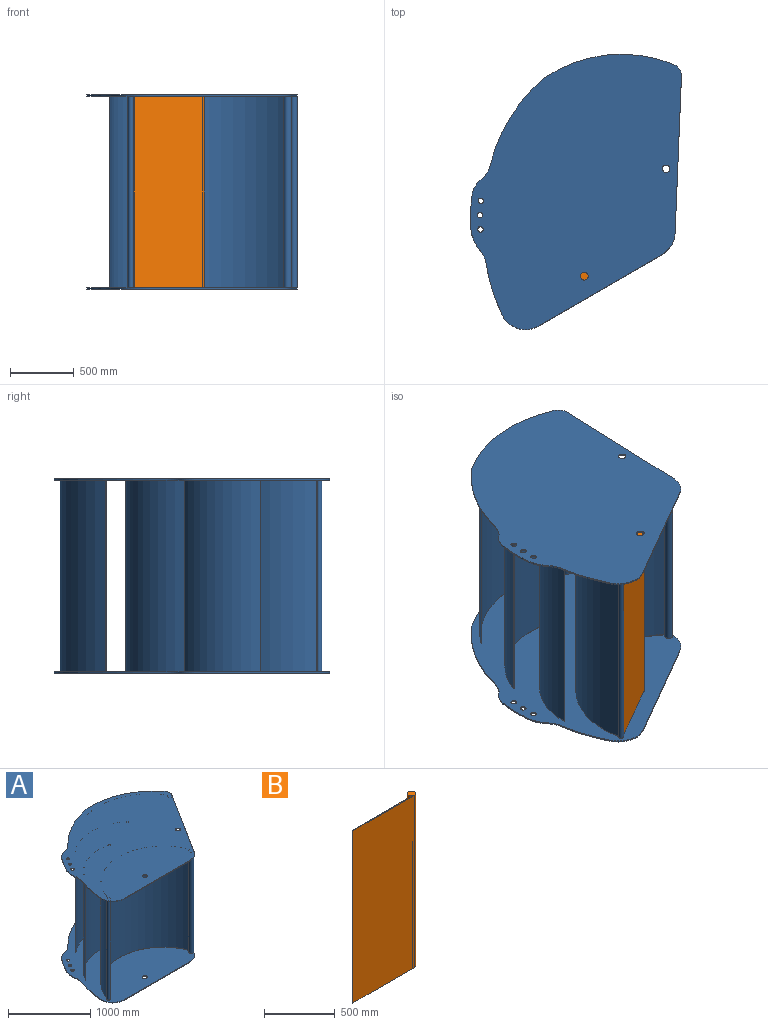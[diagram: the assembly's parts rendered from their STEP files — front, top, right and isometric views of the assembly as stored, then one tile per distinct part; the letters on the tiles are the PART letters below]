
ASSEMBLY  parts=2 mates=2
PART A: 61 faces, bbox 2164.2x1661x1520 mm
  f0: cylinder r=30.5mm len=61mm, axis (0,0,-1), area 1916.4mm2, adj f48,f49
  f1: cylinder r=29.5mm len=59mm, axis (0,0,-1), area 1853.5mm2, adj f48,f49
  f2: cylinder r=22mm len=44mm, axis (0,0,-1), area 1382.3mm2, adj f48,f49
  f3: cylinder r=22mm len=44mm, axis (0,0,-1), area 1382.3mm2, adj f48,f49
  f4: cylinder r=22mm len=44mm, axis (0,0,-1), area 1382.3mm2, adj f48,f49
  f5: cylinder r=326.18mm len=176.61mm, axis (0,0,-1), area 1797.7mm2, adj f48,f49,f50,f60
  f6: cylinder r=200mm len=212.82mm, axis (0,0,-1), area 3269.9mm2, adj f48,f49,f51,f52
  f7: cylinder r=20.5mm len=1500mm, axis (0,0,-1), area 183146.8mm2, adj f30,f44,f45,f49
  f8: cylinder r=30.5mm len=1500mm, axis (0,0,-1), area 272705.4mm2, adj f30,f44,f45,f46,f47,f49
  f9: cylinder r=15.5mm len=1500mm, axis (0,0,-1), area 135747.8mm2, adj f30,f41,f43,f49
  f10: cylinder r=15.5mm len=1500mm, axis (0,0,-1), area 136340.4mm2, adj f30,f37,f40,f49
  f11: cylinder r=30.5mm len=1500mm, axis (0,0,-1), area 274743.1mm2, adj f30,f32,f34,f35,f36,f49
  f12: cylinder r=30.5mm len=61mm, axis (0,0,-1), area 1916.4mm2, adj f30,f31
  f13: cylinder r=22mm len=44mm, axis (0,0,-1), area 1382.3mm2, adj f30,f31
  f14: cylinder r=22mm len=44mm, axis (0,0,-1), area 1382.3mm2, adj f30,f31
  f15: cylinder r=22mm len=44mm, axis (0,0,-1), area 1382.3mm2, adj f30,f31
  f16: cylinder r=29.5mm len=59mm, axis (0,0,-1), area 1853.5mm2, adj f30,f31
  f17: cylinder r=326.18mm len=176.61mm, axis (0,0,-1), area 1797.7mm2, adj f28,f29,f30,f31
  f18: cylinder r=200mm len=212.82mm, axis (0,0,-1), area 3269.9mm2, adj f19,f20,f30,f31
  f19: cylinder r=1403.06mm len=415.74mm, axis (0,0,-1), area 4273.2mm2, adj f18,f29,f30,f31
  f20: plane 1123.76x10mm, normal (0,-1,0), area 11237.6mm2, adj f18,f21,f30,f31
  f21: cylinder r=200mm len=169mm, axis (0,0,-1), area 2013.2mm2, adj f20,f22,f30,f31
  f22: plane 1036.5x655.9mm, normal (0.85,-0.53,0), area 12265.9mm2, adj f21,f23,f30,f31,f36,f47
  f23: cylinder r=100mm len=114.68mm, axis (0,0,-1), area 1222.9mm2, adj f22,f24,f30,f31
  f24: cylinder r=1074.34mm len=926.41mm, axis (0,0,-1), area 10568mm2, adj f23,f25,f30,f31
  f25: cylinder r=1282.61mm len=713.26mm, axis (0,0,-1), area 8227.7mm2, adj f24,f26,f30,f31
  f26: cylinder r=200mm len=117.51mm, axis (0,0,-1), area 1346.6mm2, adj f25,f27,f30,f31
  f27: cylinder r=186.95mm len=116.81mm, axis (0,0,-1), area 1363.1mm2, adj f26,f28,f30,f31
  f28: cylinder r=1324.47mm len=239.75mm, axis (0,0,-1), area 2828.3mm2, adj f17,f27,f30,f31
  f29: cylinder r=200mm len=107.43mm, axis (0,0,-1), area 1093.1mm2, adj f17,f19,f30,f31
  f30: plane 2164.16x1660.98mm, normal (0,0,1), area 2565292.9mm2, adj f7,f8,f9,f10,f11,f12,f13,f14
  f31: plane 2164.16x1660.98mm, normal (0,0,-1), area 2603609.2mm2, adj f12,f13,f14,f15,f16,f17,f18,f19
  f32: cylinder r=883.17mm len=1500mm, axis (0,0,-1), area 1936048.7mm2, adj f11,f30,f33,f49
  f33: plane 1500x5.5mm, normal (-0.92,-0.4,0), area 9000mm2, adj f30,f32,f34,f49
  f34: cylinder r=877.17mm len=1500mm, axis (0,0,-1), area 1914005.6mm2, adj f11,f30,f33,f49
  f35: plane 9.3x5.88mm, normal (0,0,1), area 3.7mm2, adj f11,f54
  f36: plane 9.3x5.88mm, normal (0,0,-1), area 3.7mm2, adj f11,f22
  f37: cylinder r=685.89mm len=1500mm, axis (0,0,-1), area 1444091.5mm2, adj f10,f30,f38,f49
  f38: plane 1500x4.62mm, normal (-0.77,-0.64,0), area 9000mm2, adj f30,f37,f39,f49
  f39: plane 1500x0.08mm, normal (0.65,-0.76,0), area 152.6mm2, adj f30,f38,f40,f49
  f40: cylinder r=679.89mm len=1500mm, axis (0,0,-1), area 1427930.9mm2, adj f10,f30,f39,f49
  f41: cylinder r=640.37mm len=1500mm, axis (0,0,-1), area 1242581.2mm2, adj f9,f30,f42,f49
  f42: plane 1500x5.24mm, normal (-0.49,-0.87,0), area 9000mm2, adj f30,f41,f43,f49
  f43: cylinder r=634.37mm len=1500mm, axis (0,0,-1), area 1226053.6mm2, adj f9,f30,f42,f49
  f44: cylinder r=755.25mm len=1500mm, axis (0,0,-1), area 2799788.5mm2, adj f7,f8,f30,f49
  f45: cylinder r=761.25mm len=1500mm, axis (0,0,-1), area 2838096.4mm2, adj f7,f8,f30,f49
  f46: plane 9.3x5.88mm, normal (0,0,1), area 3.7mm2, adj f8,f54
  f47: plane 9.3x5.88mm, normal (0,0,-1), area 3.7mm2, adj f8,f22
  f48: plane 2164.16x1660.98mm, normal (0,0,1), area 2603609.2mm2, adj f0,f1,f2,f3,f4,f5,f6,f50
  f49: plane 2164.16x1660.98mm, normal (0,0,-1), area 2565292.9mm2, adj f0,f1,f2,f3,f4,f5,f6,f7
  f50: cylinder r=200mm len=107.43mm, axis (0,0,-1), area 1093.1mm2, adj f5,f48,f49,f51
  f51: cylinder r=1403.06mm len=415.74mm, axis (0,0,-1), area 4273.2mm2, adj f6,f48,f49,f50
  f52: plane 1123.76x10mm, normal (0,-1,0), area 11237.6mm2, adj f6,f48,f49,f53
  f53: cylinder r=200mm len=169mm, axis (0,0,-1), area 2013.2mm2, adj f48,f49,f52,f54
  f54: plane 1036.5x655.9mm, normal (0.85,-0.53,0), area 12265.9mm2, adj f35,f46,f48,f49,f53,f55
  f55: cylinder r=100mm len=114.68mm, axis (0,0,-1), area 1222.9mm2, adj f48,f49,f54,f56
  f56: cylinder r=1074.34mm len=926.41mm, axis (0,0,-1), area 10568mm2, adj f48,f49,f55,f57
  f57: cylinder r=1282.61mm len=713.26mm, axis (0,0,-1), area 8227.7mm2, adj f48,f49,f56,f58
  f58: cylinder r=200mm len=117.51mm, axis (0,0,-1), area 1346.6mm2, adj f48,f49,f57,f59
  f59: cylinder r=186.95mm len=116.81mm, axis (0,0,-1), area 1363.1mm2, adj f48,f49,f58,f60
  f60: cylinder r=1324.47mm len=239.75mm, axis (0,0,-1), area 2828.3mm2, adj f5,f48,f49,f59
PART B: 6 faces, bbox 646.3x61x1490 mm
  f0: cylinder r=30.5mm len=1490mm, axis (0,0,-1), area 256544.7mm2, adj f1,f2,f4,f5
  f1: plane 1490x615.77mm, normal (0,-1,0), area 917501.9mm2, adj f0,f3,f4,f5
  f2: plane 1490x597.61mm, normal (0,1,0), area 890434.7mm2, adj f0,f3,f4,f5
  f3: plane 1490x6mm, normal (-1,0,0), area 8940mm2, adj f1,f2,f4,f5
  f4: plane 646.27x61mm, normal (0,0,1), area 6542.9mm2, adj f0,f1,f2,f3
  f5: plane 646.27x61mm, normal (0,0,-1), area 6542.9mm2, adj f0,f1,f2,f3
PLACE A rot(axis=(0,0,1),30deg) t=(0,0,-10)mm
PLACE B rot(axis=(0,0,1),30deg) t=(0,0,-10)mm
MATE planar A.f0 <-> B.f0  axis (0,0,-1) through (-640.96,-840.78,750)mm
MATE revolute A.f0 <-> B.f0  axis (0,0,-1) through (-640.96,-840.78,750)mm
